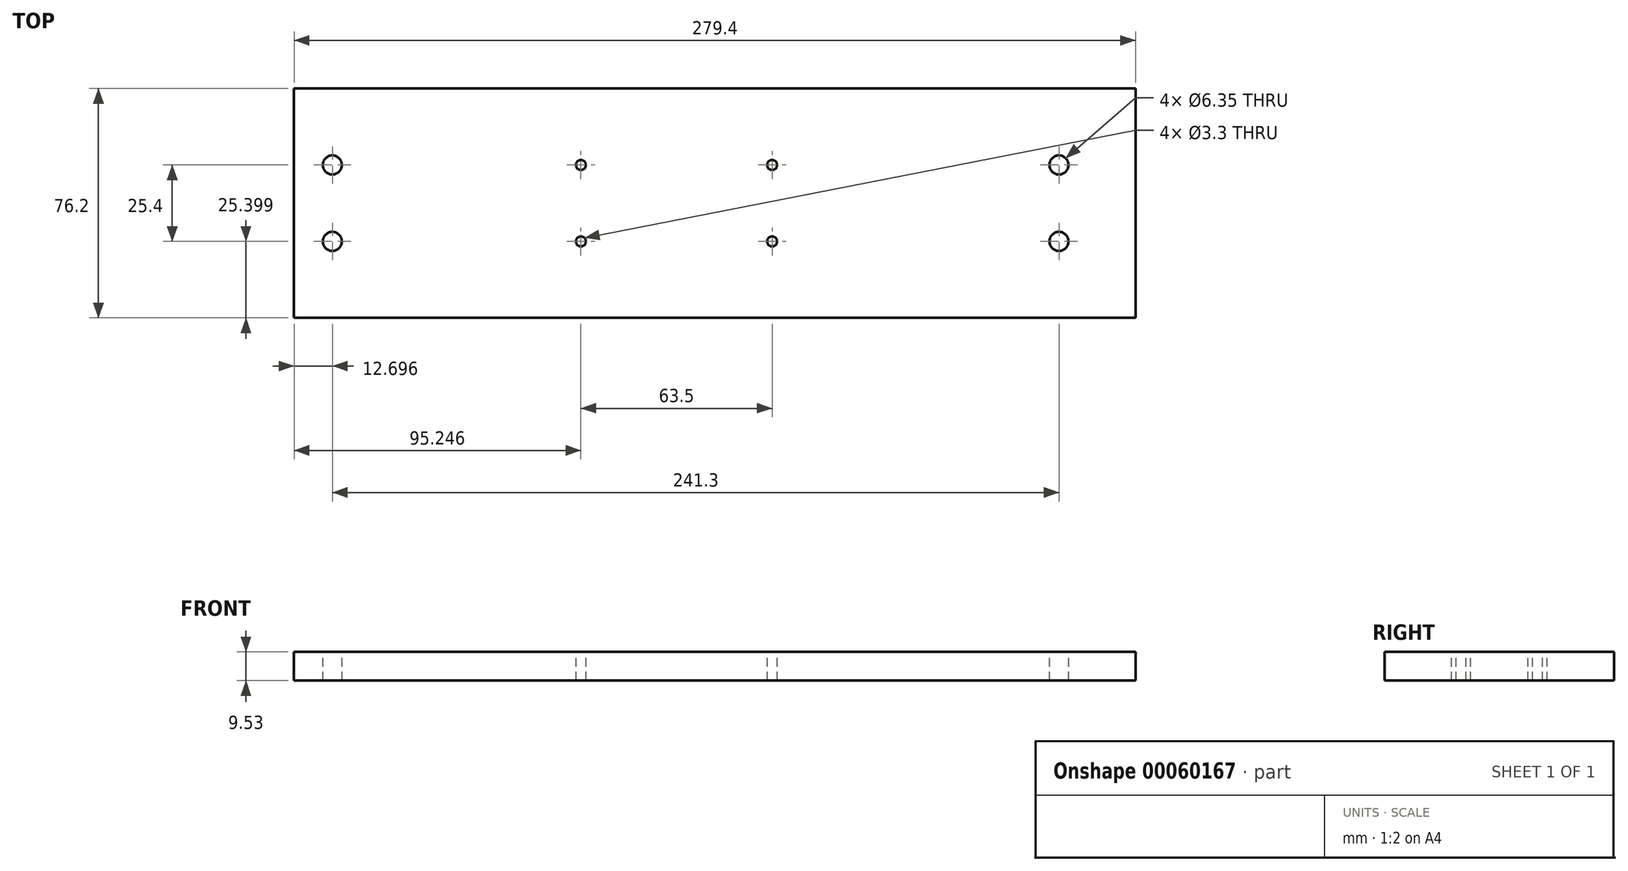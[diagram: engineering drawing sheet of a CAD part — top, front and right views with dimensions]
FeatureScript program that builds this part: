
annotation { "Feature Type Name" : "Feature", "Feature Type Description" : "" }
export const myFeature = defineFeature(function(context is Context, id is Id, definition is map)
    precondition{}
    {
        {
            var Q0;
            Q0=qCreatedBy(makeId("Top.planeOp"),FACE);
            var sketch = newSketch(context, id + "F0", { "sketchPlane" : qUnion([Q0])});
            skLineSegment(sketch, "E0.bottom", {"start": v(-142.5, 58.67) * mm, "end": v(136.9, 58.67) * mm});
            skLineSegment(sketch, "E0.top", {"start": v(-142.5, -17.53) * mm, "end": v(136.9, -17.53) * mm});
            skLineSegment(sketch, "E0.left", {"start": v(-142.5, 58.67) * mm, "end": v(-142.5, -17.53) * mm});
            skLineSegment(sketch, "E0.right", {"start": v(136.9, 58.67) * mm, "end": v(136.9, -17.53) * mm});
            skSolve(sketch);
        }
        {
            var Q0;
            Q0 = qSketchRegion(id + "F0", true);
            extrude(context, id + "F1", {"entities" : qUnion([Q0]), "depth" : 9.52 * mm});
        }
        {
            var Q0;
            Q0=makeQuery(id+"F1.opExtrude","CAP_FACE",FACE,{"disambiguationData":[OSD([sQuery(id+"F0.wireOp",EDGE,"E0.bottom"),sQuery(id+"F0.wireOp",EDGE,"E0.top"),sQuery(id+"F0.wireOp",EDGE,"E0.left"),sQuery(id+"F0.wireOp",EDGE,"E0.right")])],"isStart":false});
            var sketch = newSketch(context, id + "F2", { "sketchPlane" : qUnion([Q0])});
            skCircle(sketch, "E1", {"center": v(-129.8, 33.27) * mm, "radius": 3.18 * mm});
            skCircle(sketch, "E2.MirrorC", {"center": v(-129.8, 7.87) * mm, "radius": 3.18 * mm});
            skCircle(sketch, "E3", {"center": v(111.5, 33.27) * mm, "radius": 3.18 * mm});
            skCircle(sketch, "E4.MirrorC", {"center": v(111.5, 7.87) * mm, "radius": 3.18 * mm});
            skCircle(sketch, "E5", {"center": v(-47.25, 33.27) * mm, "radius": 1.65 * mm});
            skLineSegment(sketch, "E6", {"start": v(-142.5, 20.57) * mm, "end": v(-125.53, 20.57) * mm});
            skCircle(sketch, "E7.MirrorC", {"center": v(-47.25, 7.87) * mm, "radius": 1.65 * mm});
            skCircle(sketch, "E8", {"center": v(16.25, 33.27) * mm, "radius": 1.65 * mm});
            skCircle(sketch, "E9.MirrorC", {"center": v(16.25, 7.87) * mm, "radius": 1.65 * mm});
            skSolve(sketch);
        }
        {
            var Q0;
            Q0 = qSketchRegion(id + "F2", true);
            extrude(context, id + "F3", {"entities" : qUnion([Q0]), "operationType" : NewBodyOperationType.REMOVE, "oppositeDirection" : true, "depth" : 9.52 * mm});
        }
    });
